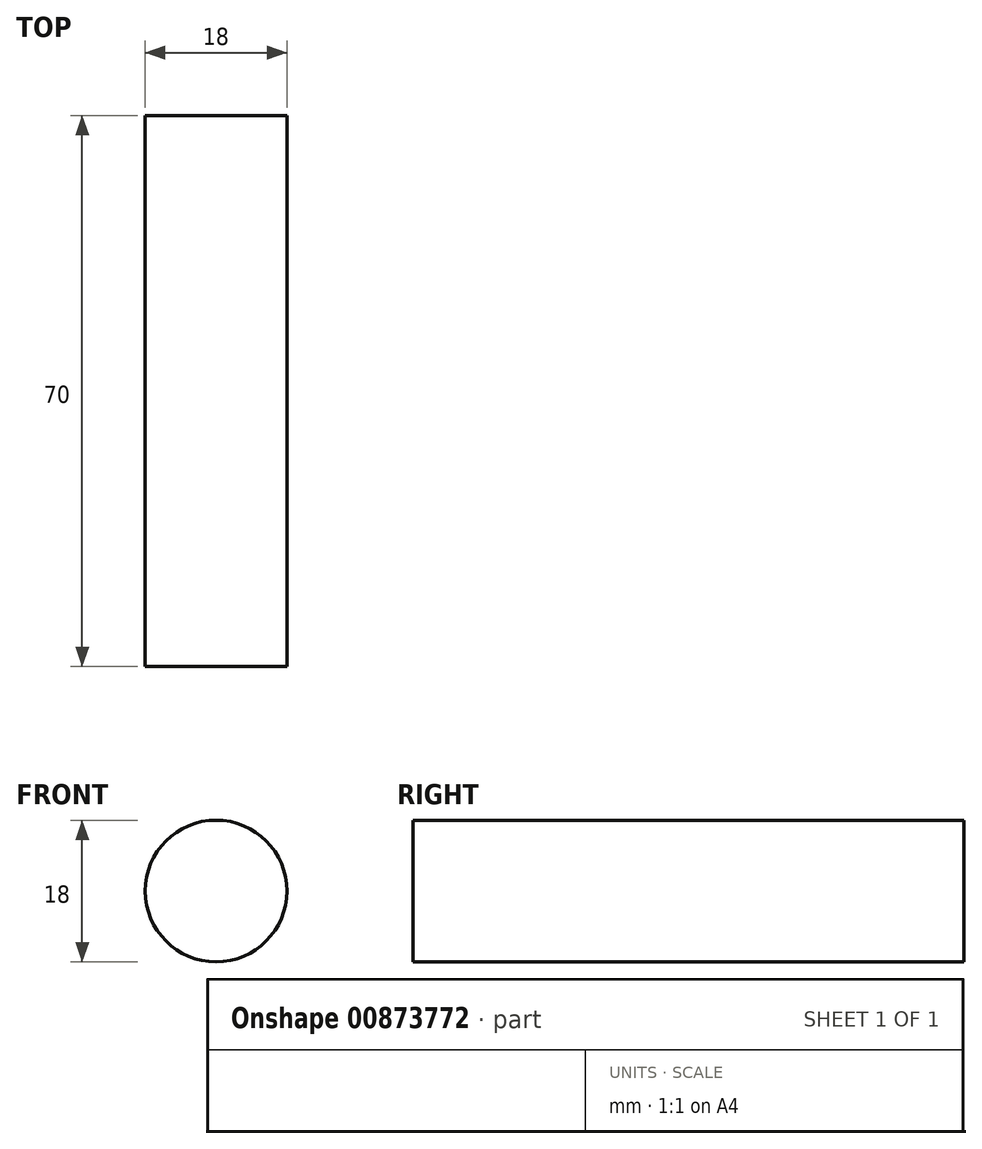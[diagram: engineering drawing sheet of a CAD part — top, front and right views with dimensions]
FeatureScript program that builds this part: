
annotation { "Feature Type Name" : "Feature", "Feature Type Description" : "" }
export const myFeature = defineFeature(function(context is Context, id is Id, definition is map)
    precondition{}
    {
        {
            var Q0;
            Q0=qCreatedBy(makeId("Front.planeOp"),FACE);
            var sketch = newSketch(context, id + "F0", { "sketchPlane" : qUnion([Q0])});
            skCircle(sketch, "E0", {"center": v(0, 0) * mm, "radius": 9 * mm});
            skSolve(sketch);
        }
        {
            var Q0;
            Q0 = qSketchRegion(id + "F0", true);
            extrude(context, id + "F1", {"entities" : qUnion([Q0]), "depth" : 70 * mm, "offsetDistance" : 25 * mm});
        }
    });
